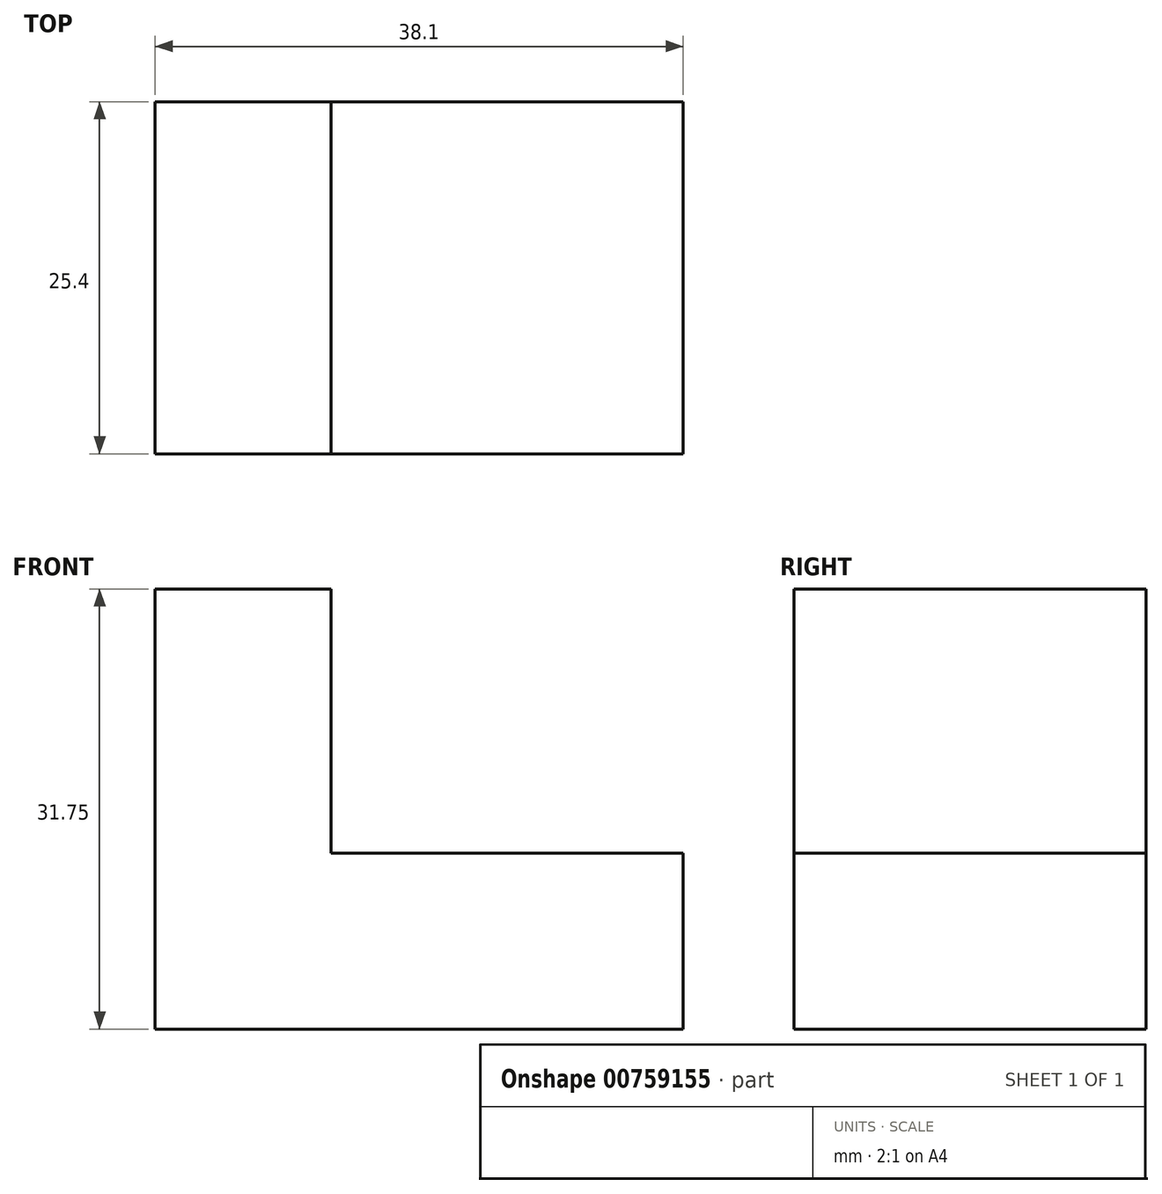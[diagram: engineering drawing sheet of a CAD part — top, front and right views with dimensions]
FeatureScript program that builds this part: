
annotation { "Feature Type Name" : "Feature", "Feature Type Description" : "" }
export const myFeature = defineFeature(function(context is Context, id is Id, definition is map)
    precondition{}
    {
        {
            var Q0;
            Q0=qCreatedBy(makeId("Front.planeOp"),FACE);
            var sketch = newSketch(context, id + "F0", { "sketchPlane" : qUnion([Q0])});
            skLineSegment(sketch, "E0", {"start": v(0, 0) * mm, "end": v(0, 31.75) * mm});
            skLineSegment(sketch, "E1", {"start": v(0, 31.75) * mm, "end": v(12.7, 31.75) * mm});
            skLineSegment(sketch, "E2", {"start": v(12.7, 31.75) * mm, "end": v(12.7, 12.7) * mm});
            skLineSegment(sketch, "E3", {"start": v(12.7, 12.7) * mm, "end": v(38.1, 12.7) * mm});
            skLineSegment(sketch, "E4", {"start": v(0, 0) * mm, "end": v(38.1, 0) * mm});
            skLineSegment(sketch, "E5", {"start": v(38.1, 0) * mm, "end": v(38.1, 12.7) * mm});
            skSolve(sketch);
        }
        {
            var Q0;
            Q0=makeQuery(id+"F0.imprint","IMPRINT",FACE,{"disambiguationData":[TD([[makeQuery(id+"F0.imprint","IMPRINT",EDGE,{"derivedFrom":sQuery(id+"F0.wireOp",EDGE,"E0")}),-1.0]])]});
            extrude(context, id + "F1", {"entities" : qUnion([Q0]), "depth" : 25.4 * mm, "offsetDistance" : 25.4 * mm});
        }
    });
